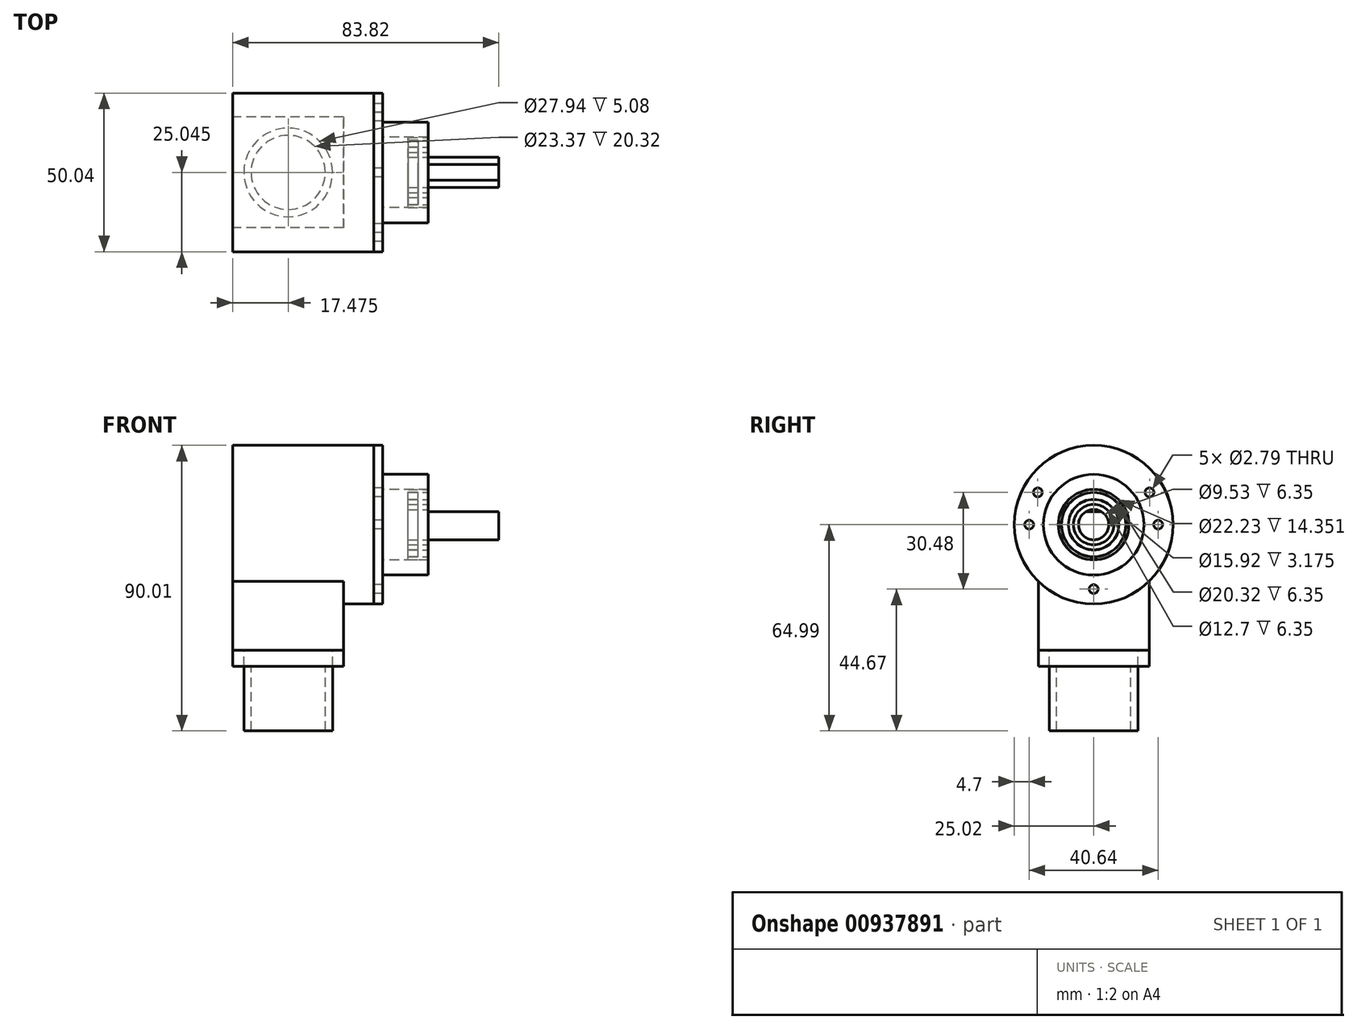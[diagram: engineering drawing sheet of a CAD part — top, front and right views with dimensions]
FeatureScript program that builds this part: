
annotation { "Feature Type Name" : "Feature", "Feature Type Description" : "" }
export const myFeature = defineFeature(function(context is Context, id is Id, definition is map)
    precondition{}
    {
        {
            var Q0;
            Q0=qCreatedBy(makeId("Right.planeOp"),FACE);
            var sketch = newSketch(context, id + "F0", { "sketchPlane" : qUnion([Q0])});
            skCircle(sketch, "E0", {"center": v(0, 0) * mm, "radius": 25 * mm});
            skCircle(sketch, "E1", {"center": v(20.32, 0) * mm, "radius": 1.4 * mm});
            skCircle(sketch, "E2", {"center": v(-20.32, 0) * mm, "radius": 1.4 * mm});
            skPoint(sketch, "E3", {"position": v(0, -20.32) * mm});
            skPoint(sketch, "E4.1.0", {"position": v(17.6, 10.16) * mm});
            skPoint(sketch, "E4.2.0", {"position": v(-17.6, 10.16) * mm});
            skCircle(sketch, "E5", {"center": v(0, -20.32) * mm, "radius": 1.4 * mm});
            skCircle(sketch, "E6", {"center": v(-17.6, 10.16) * mm, "radius": 1.4 * mm});
            skCircle(sketch, "E7", {"center": v(17.6, 10.16) * mm, "radius": 1.4 * mm});
            skSolve(sketch);
        }
        {
            var Q0;
            Q0=makeQuery(id+"F0.imprint","IMPRINT",FACE,{"disambiguationData":[TD([[makeQuery(id+"F0.imprint","IMPRINT",EDGE,{"derivedFrom":sQuery(id+"F0.wireOp",EDGE,"E0")}),1.0]])]});
            extrude(context, id + "F1", {"entities" : qUnion([Q0]), "depth" : 2.8 * mm, "offsetDistance" : 25.4 * mm});
        }
        {
            var Q0;
            Q0=makeQuery(id+"F1.opExtrude","CAP_FACE",FACE,{"disambiguationData":[OSD([sQuery(id+"F0.wireOp",EDGE,"E0"),sQuery(id+"F0.wireOp",EDGE,"E1"),sQuery(id+"F0.wireOp",EDGE,"E2")])],"isStart":false});
            var sketch = newSketch(context, id + "F2", { "sketchPlane" : qUnion([Q0])});
            skCircle(sketch, "E8", {"center": v(0, 0) * mm, "radius": 15.88 * mm});
            skCircle(sketch, "E9", {"center": v(0, 0) * mm, "radius": 11.11 * mm});
            skSolve(sketch);
        }
        {
            var Q0;
            Q0=makeQuery(id+"F2.imprint","IMPRINT",FACE,{"disambiguationData":[TD([[makeQuery(id+"F2.imprint","IMPRINT",EDGE,{"derivedFrom":sQuery(id+"F2.wireOp",EDGE,"E8")}),1.0]])]});
            extrude(context, id + "F3", {"entities" : qUnion([Q0]), "operationType" : NewBodyOperationType.ADD, "depth" : 14.35 * mm, "offsetDistance" : 25.4 * mm});
        }
        {
            var Q0;
            Q0=makeQuery(id+"F3.opExtrude","CAP_FACE",FACE,{"disambiguationData":[OSD([sQuery(id+"F2.wireOp",EDGE,"E8"),sQuery(id+"F2.wireOp",EDGE,"E9")])],"isStart":false});
            var sketch = newSketch(context, id + "F4", { "sketchPlane" : qUnion([Q0])});
            skLineSegment(sketch, "E10", {"start": v(-2.46, 4.08) * mm, "end": v(2.46, 4.08) * mm});
            skArc(sketch, "E11", {"start": v(-2.46, 4.08) * mm, "mid": v(0, -4.76) * mm, "end": v(2.46, 4.08) * mm});
            skSolve(sketch);
        }
        {
            var Q0;
            Q0=makeQuery(id+"F4.imprint","IMPRINT",FACE,{"disambiguationData":[TD([[makeQuery(id+"F4.imprint","IMPRINT",EDGE,{"derivedFrom":sQuery(id+"F4.wireOp",EDGE,"E10")}),-1.0]])]});
            extrude(context, id + "F5", {"entities" : qUnion([Q0]), "depth" : 22.22 * mm, "offsetDistance" : 25.4 * mm});
        }
        {
            var Q0;
            Q0=qCreatedBy(makeId("Right.planeOp"),FACE);
            var sketch = newSketch(context, id + "F6", { "sketchPlane" : qUnion([Q0])});
            skCircle(sketch, "E12", {"center": v(0, 0) * mm, "radius": 25.02 * mm});
            skSolve(sketch);
        }
        {
            var Q0;
            Q0=qSketchRegion(id+"F6",true);
            extrude(context, id + "F7", {"entities" : qUnion([Q0]), "depth" : -44.45 * mm, "offsetDistance" : 25.4 * mm});
        }
        {
            var Q0;
            Q0=makeQuery(id+"F7.opExtrude","CAP_FACE",FACE,{"disambiguationData":[OSD([sQuery(id+"F6.wireOp",EDGE,"E12")])],"isStart":false});
            var sketch = newSketch(context, id + "F8", { "sketchPlane" : qUnion([Q0])});
            skLineSegment(sketch, "E13", {"start": v(-17.48, -39.59) * mm, "end": v(17.45, -39.59) * mm});
            skLineSegment(sketch, "E14", {"start": v(-17.48, -39.59) * mm, "end": v(-17.48, -38.12) * mm});
            skLineSegment(sketch, "E15", {"start": v(-17.48, -17.9) * mm, "end": v(-17.48, -39.59) * mm});
            skLineSegment(sketch, "E16", {"start": v(17.45, -39.59) * mm, "end": v(17.45, -38.68) * mm});
            skLineSegment(sketch, "E17", {"start": v(17.45, -17.93) * mm, "end": v(17.45, -39.59) * mm});
            skSolve(sketch);
        }
        {
            var Q0;
            {var subQ0=sQuery(id+"F8.wireOp",EDGE,"E13");Q0=makeQuery(id+"F8.imprint","IMPRINT",FACE,{"disambiguationData":[TD([[makeQuery(id+"F8.imprint","IMPRINT",EDGE,{"derivedFrom":subQ0}),1.0]])]});}
            extrude(context, id + "F9", {"entities" : qUnion([Q0]), "operationType" : NewBodyOperationType.ADD, "oppositeDirection" : true, "depth" : 34.92 * mm, "offsetDistance" : 25.4 * mm});
        }
        {
            var Q0;
            Q0=makeQuery(id+"F3.opExtrude","CAP_FACE",FACE,{"disambiguationData":[OSD([sQuery(id+"F2.wireOp",EDGE,"E8"),sQuery(id+"F2.wireOp",EDGE,"E9")])],"isStart":false});
            var sketch = newSketch(context, id + "F10", { "sketchPlane" : qUnion([Q0])});
            skCircle(sketch, "E18", {"center": v(0, 0) * mm, "radius": 4.76 * mm});
            skCircle(sketch, "E19", {"center": v(0, 0) * mm, "radius": 6.35 * mm});
            skSolve(sketch);
        }
        {
            var Q0;
            Q0=makeQuery(id+"F10.imprint","IMPRINT",FACE,{"disambiguationData":[TD([[makeQuery(id+"F10.imprint","IMPRINT",EDGE,{"derivedFrom":sQuery(id+"F10.wireOp",EDGE,"E18")}),-1.0]])]});
            extrude(context, id + "F11", {"entities" : qUnion([Q0]), "oppositeDirection" : true, "depth" : 6.35 * mm, "offsetDistance" : 25.4 * mm});
        }
        {
            var Q0;
            Q0=makeQuery(id+"F3.opExtrude","CAP_FACE",FACE,{"disambiguationData":[OSD([sQuery(id+"F2.wireOp",EDGE,"E8"),sQuery(id+"F2.wireOp",EDGE,"E9")])],"isStart":false});
            var sketch = newSketch(context, id + "F12", { "sketchPlane" : qUnion([Q0])});
            skCircle(sketch, "E20", {"center": v(0, 0) * mm, "radius": 7.94 * mm});
            skCircle(sketch, "E21", {"center": v(0, 0) * mm, "radius": 6.35 * mm});
            skSolve(sketch);
        }
        {
            var Q0;
            Q0=makeQuery(id+"F12.imprint","IMPRINT",FACE,{"disambiguationData":[TD([[makeQuery(id+"F12.imprint","IMPRINT",EDGE,{"derivedFrom":sQuery(id+"F12.wireOp",EDGE,"E20")}),1.0]])]});
            extrude(context, id + "F13", {"entities" : qUnion([Q0]), "oppositeDirection" : true, "depth" : 6.35 * mm, "offsetDistance" : 25.4 * mm});
        }
        {
            var Q0;
            Q0=makeQuery(id+"F3.opExtrude","CAP_FACE",FACE,{"disambiguationData":[OSD([sQuery(id+"F2.wireOp",EDGE,"E8"),sQuery(id+"F2.wireOp",EDGE,"E9")])],"isStart":false});
            var sketch = newSketch(context, id + "F14", { "sketchPlane" : qUnion([Q0])});
            skCircle(sketch, "E22", {"center": v(0, 0) * mm, "radius": 11.08 * mm});
            skCircle(sketch, "E23", {"center": v(0, 0) * mm, "radius": 10.16 * mm});
            skSolve(sketch);
        }
        {
            var Q0;
            Q0=makeQuery(id+"F14.imprint","IMPRINT",FACE,{"disambiguationData":[TD([[makeQuery(id+"F14.imprint","IMPRINT",EDGE,{"derivedFrom":sQuery(id+"F14.wireOp",EDGE,"E22")}),1.0]])]});
            extrude(context, id + "F15", {"entities" : qUnion([Q0]), "oppositeDirection" : true, "depth" : 6.35 * mm, "offsetDistance" : 25.4 * mm});
        }
        {
            var Q0;
            Q0=makeQuery(id+"F3.opExtrude","CAP_FACE",FACE,{"disambiguationData":[OSD([sQuery(id+"F2.wireOp",EDGE,"E8"),sQuery(id+"F2.wireOp",EDGE,"E9")])],"isStart":false});
            var sketch = newSketch(context, id + "F16", { "sketchPlane" : qUnion([Q0])});
            skCircle(sketch, "E24", {"center": v(0, 0) * mm, "radius": 10.14 * mm});
            skCircle(sketch, "E25", {"center": v(0, 0) * mm, "radius": 7.96 * mm});
            skSolve(sketch);
        }
        {
            var Q0;
            Q0=makeQuery(id+"F16.imprint","IMPRINT",FACE,{"disambiguationData":[TD([[makeQuery(id+"F16.imprint","IMPRINT",EDGE,{"derivedFrom":sQuery(id+"F16.wireOp",EDGE,"E24")}),1.0]])]});
            extrude(context, id + "F17", {"entities" : qUnion([Q0]), "depth" : 3.17 * mm, "offsetDistance" : 25.4 * mm});
        }
        {
            var Q0;
            Q0=makeQuery(id+"F17.opExtrude","SWEPT_BODY",BODY,{"disambiguationData":[OSD([sQuery(id+"F16.wireOp",EDGE,"E24"),sQuery(id+"F16.wireOp",EDGE,"E25")])]});
            var Q1;
            Q1=makeQuery(id+"F3.opExtrude","CAP_FACE",FACE,{"disambiguationData":[OSD([sQuery(id+"F2.wireOp",EDGE,"E8"),sQuery(id+"F2.wireOp",EDGE,"E9")])],"isStart":false});
            transform(context, id + "F18", {"entities" : qUnion([Q0]), "transformType" : TransformType.TRANSLATION_DISTANCE, "transformDirection" : qUnion([Q1]), "distance" : 6.35 * mm, "oppositeDirection" : true, "makeCopy" : false});
        }
        {
            var Q0;
            Q0=makeQuery(id+"F9.opExtrude","SWEPT_FACE",FACE,{"disambiguationData":[OSD([sQuery(id+"F8.wireOp",EDGE,"E13")])]});
            var sketch = newSketch(context, id + "F19", { "sketchPlane" : qUnion([Q0])});
            skLineSegment(sketch, "E26.bottom", {"start": v(-44.45, 17.45) * mm, "end": v(-9.52, 17.45) * mm});
            skLineSegment(sketch, "E26.top", {"start": v(-44.45, -17.48) * mm, "end": v(-9.52, -17.48) * mm});
            skLineSegment(sketch, "E26.left", {"start": v(-44.45, 17.45) * mm, "end": v(-44.45, -17.48) * mm});
            skLineSegment(sketch, "E26.right", {"start": v(-9.52, 17.45) * mm, "end": v(-9.52, -17.48) * mm});
            skCircle(sketch, "E27", {"center": v(-26.97, -0.03) * mm, "radius": 13.97 * mm});
            skSolve(sketch);
        }
        {
            var Q0;
            Q0=makeQuery(id+"F19.imprint","IMPRINT",FACE,{"disambiguationData":[TD([[makeQuery(id+"F19.imprint","IMPRINT",EDGE,{"derivedFrom":sQuery(id+"F19.wireOp",EDGE,"E26.bottom")}),1.0]])]});
            extrude(context, id + "F20", {"entities" : qUnion([Q0]), "depth" : 5.08 * mm, "offsetDistance" : 25.4 * mm});
        }
        {
            var Q0;
            Q0=makeQuery(id+"F20.opExtrude","CAP_FACE",FACE,{"disambiguationData":[OSD([sQuery(id+"F19.wireOp",EDGE,"E26.bottom"),sQuery(id+"F19.wireOp",EDGE,"E26.top"),sQuery(id+"F19.wireOp",EDGE,"E26.left"),sQuery(id+"F19.wireOp",EDGE,"E26.right"),sQuery(id+"F19.wireOp",EDGE,"E27")])],"isStart":false});
            var sketch = newSketch(context, id + "F21", { "sketchPlane" : qUnion([Q0])});
            skCircle(sketch, "E28", {"center": v(-26.97, -0.03) * mm, "radius": 11.68 * mm});
            skSolve(sketch);
        }
        {
            var Q0;
            Q0=makeQuery(id+"F21.imprint","IMPRINT",FACE,{"disambiguationData":[TD([[makeQuery(id+"F21.imprint","IMPRINT",EDGE,{"derivedFrom":sQuery(id+"F21.wireOp",EDGE,"E28")}),-1.0]])]});
            extrude(context, id + "F22", {"entities" : qUnion([Q0]), "depth" : 20.32 * mm, "offsetDistance" : 25.4 * mm});
        }
    });
